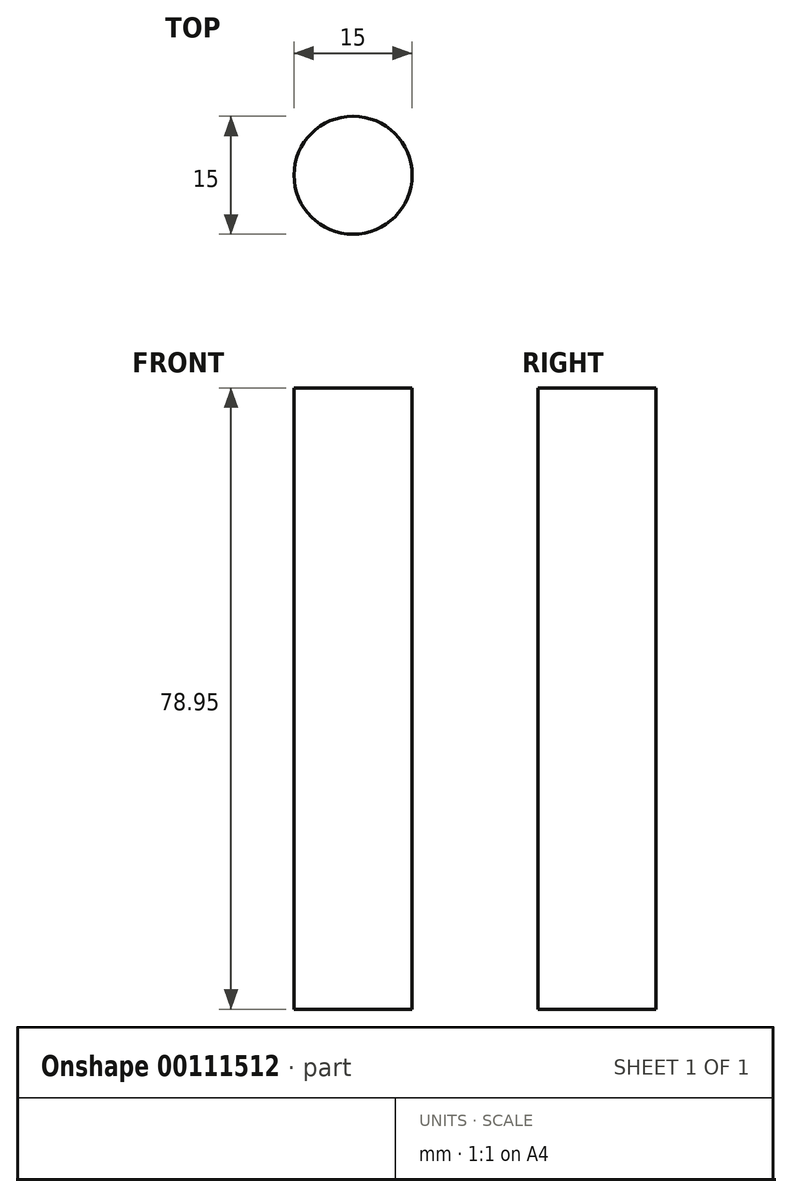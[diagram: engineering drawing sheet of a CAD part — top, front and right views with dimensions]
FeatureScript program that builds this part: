
annotation { "Feature Type Name" : "Feature", "Feature Type Description" : "" }
export const myFeature = defineFeature(function(context is Context, id is Id, definition is map)
    precondition{}
    {
        {
            var Q0;
            Q0=qCreatedBy(makeId("Top.planeOp"),FACE);
            var sketch = newSketch(context, id + "F0", { "sketchPlane" : qUnion([Q0])});
            skCircle(sketch, "E0", {"center": v(0, 0) * mm, "radius": 7.5 * mm});
            skSolve(sketch);
        }
        {
            var Q0;
            Q0 = qSketchRegion(id + "F0", true);
            extrude(context, id + "F1", {"entities" : qUnion([Q0]), "depth" : 78.95 * mm});
        }
    });
